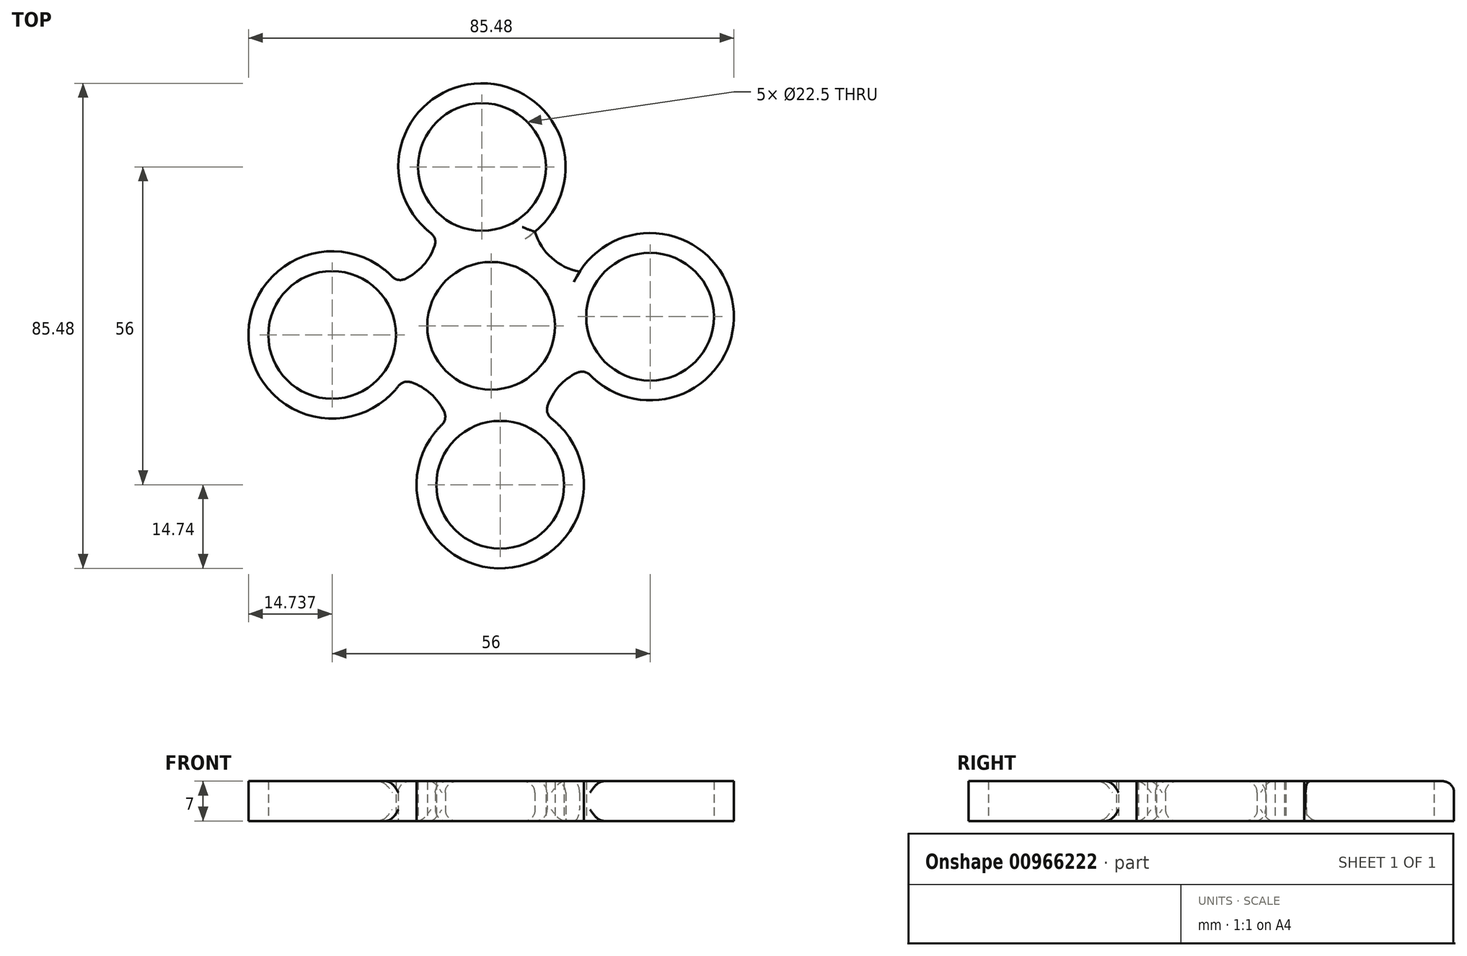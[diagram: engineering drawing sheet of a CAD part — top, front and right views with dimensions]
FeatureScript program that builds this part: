
annotation { "Feature Type Name" : "Feature", "Feature Type Description" : "" }
export const myFeature = defineFeature(function(context is Context, id is Id, definition is map)
    precondition{}
    {
        {
            var Q0;
            Q0=qCreatedBy(makeId("Top.planeOp"),FACE);
            var sketch = newSketch(context, id + "F0", { "sketchPlane" : qUnion([Q0])});
            skCircle(sketch, "E0", {"center": v(-7.42, 16.64) * mm, "radius": 11.25 * mm});
            skCircle(sketch, "E1", {"center": v(-9.03, 44.64) * mm, "radius": 11.25 * mm});
            skCircle(sketch, "E2.1.0", {"center": v(-35.42, 15.03) * mm, "radius": 11.25 * mm});
            skCircle(sketch, "E2.2.0", {"center": v(-5.82, -11.36) * mm, "radius": 11.25 * mm});
            skCircle(sketch, "E2.3.0", {"center": v(20.58, 18.25) * mm, "radius": 11.25 * mm});
            skArc(sketch, "E3", {"start": v(-28.83, 24.15) * mm, "mid": v(-19.39, 27.28) * mm, "end": v(-17.29, 37) * mm});
            skArc(sketch, "E4.1.0", {"start": v(-14.93, -4.76) * mm, "mid": v(-18.06, 4.67) * mm, "end": v(-27.78, 6.78) * mm});
            skArc(sketch, "E4.2.0", {"start": v(13.98, 9.13) * mm, "mid": v(4.54, 6) * mm, "end": v(2.44, -3.72) * mm});
            skArc(sketch, "E4.3.0", {"start": v(0.08, 38.04) * mm, "mid": v(3.22, 28.6) * mm, "end": v(12.94, 26.5) * mm});
            skCircle(sketch, "E5", {"center": v(-9.03, 44.64) * mm, "radius": 14.74 * mm});
            skCircle(sketch, "E6.1.0", {"center": v(-35.42, 15.03) * mm, "radius": 14.74 * mm});
            skCircle(sketch, "E6.2.0", {"center": v(-5.82, -11.36) * mm, "radius": 14.74 * mm});
            skCircle(sketch, "E6.3.0", {"center": v(20.58, 18.25) * mm, "radius": 14.74 * mm});
            skSolve(sketch);
        }
        {
            var Q0;
            {var subQ0=sQuery(id+"F0.wireOp",EDGE,"E3");var subQ1=sQuery(id+"F0.wireOp",EDGE,"E2.1.0");var subQ2=makeQuery(id+"F0.imprint","INTERSECT",VERTEX,{"derivedFrom":[subQ1,subQ0]});Q0=makeQuery(id+"F0.imprint","IMPRINT",FACE,{"disambiguationData":[TD([[makeQuery(id+"F0.imprint","IMPRINT",EDGE,{"disambiguationData":[TD([[subQ2,1.0]])],"derivedFrom":subQ1}),-1.0]])]});}
            var Q1;
            {var subQ0=sQuery(id+"F0.wireOp",EDGE,"E3");var subQ1=sQuery(id+"F0.wireOp",EDGE,"E2.1.0");var subQ2=makeQuery(id+"F0.imprint","INTERSECT",VERTEX,{"derivedFrom":[subQ1,subQ0]});Q1=makeQuery(id+"F0.imprint","IMPRINT",FACE,{"disambiguationData":[TD([[makeQuery(id+"F0.imprint","IMPRINT",EDGE,{"disambiguationData":[TD([[subQ2,-1.0]])],"derivedFrom":subQ1}),-1.0]])]});}
            var Q2;
            Q2=makeQuery(id+"F0.imprint","IMPRINT",FACE,{"disambiguationData":[TD([[makeQuery(id+"F0.imprint","IMPRINT",EDGE,{"derivedFrom":sQuery(id+"F0.wireOp",EDGE,"E0")}),-1.0]])]});
            var Q3;
            {var subQ0=sQuery(id+"F0.wireOp",EDGE,"E3");var subQ1=sQuery(id+"F0.wireOp",EDGE,"E1");var subQ2=makeQuery(id+"F0.imprint","INTERSECT",VERTEX,{"derivedFrom":[subQ1,subQ0]});Q3=makeQuery(id+"F0.imprint","IMPRINT",FACE,{"disambiguationData":[TD([[makeQuery(id+"F0.imprint","IMPRINT",EDGE,{"disambiguationData":[TD([[subQ2,-1.0]])],"derivedFrom":subQ1}),-1.0]])]});}
            var Q4;
            {var subQ0=sQuery(id+"F0.wireOp",EDGE,"E3");var subQ1=sQuery(id+"F0.wireOp",EDGE,"E1");var subQ2=makeQuery(id+"F0.imprint","INTERSECT",VERTEX,{"derivedFrom":[subQ1,subQ0]});Q4=makeQuery(id+"F0.imprint","IMPRINT",FACE,{"disambiguationData":[TD([[makeQuery(id+"F0.imprint","IMPRINT",EDGE,{"disambiguationData":[TD([[subQ2,1.0]])],"derivedFrom":subQ1}),-1.0]])]});}
            var Q5;
            {var subQ0=sQuery(id+"F0.wireOp",EDGE,"E4.2.0");var subQ1=sQuery(id+"F0.wireOp",EDGE,"E2.3.0");var subQ2=makeQuery(id+"F0.imprint","INTERSECT",VERTEX,{"derivedFrom":[subQ1,subQ0]});Q5=makeQuery(id+"F0.imprint","IMPRINT",FACE,{"disambiguationData":[TD([[makeQuery(id+"F0.imprint","IMPRINT",EDGE,{"disambiguationData":[TD([[subQ2,-1.0]])],"derivedFrom":subQ1}),-1.0]])]});}
            var Q6;
            {var subQ0=sQuery(id+"F0.wireOp",EDGE,"E4.2.0");var subQ1=sQuery(id+"F0.wireOp",EDGE,"E2.3.0");var subQ2=makeQuery(id+"F0.imprint","INTERSECT",VERTEX,{"derivedFrom":[subQ1,subQ0]});Q6=makeQuery(id+"F0.imprint","IMPRINT",FACE,{"disambiguationData":[TD([[makeQuery(id+"F0.imprint","IMPRINT",EDGE,{"disambiguationData":[TD([[subQ2,1.0]])],"derivedFrom":subQ1}),-1.0]])]});}
            var Q7;
            {var subQ0=sQuery(id+"F0.wireOp",EDGE,"E4.1.0");var subQ1=sQuery(id+"F0.wireOp",EDGE,"E2.2.0");var subQ2=makeQuery(id+"F0.imprint","INTERSECT",VERTEX,{"derivedFrom":[subQ1,subQ0]});Q7=makeQuery(id+"F0.imprint","IMPRINT",FACE,{"disambiguationData":[TD([[makeQuery(id+"F0.imprint","IMPRINT",EDGE,{"disambiguationData":[TD([[subQ2,1.0]])],"derivedFrom":subQ1}),-1.0]])]});}
            var Q8;
            {var subQ0=sQuery(id+"F0.wireOp",EDGE,"E4.1.0");var subQ1=sQuery(id+"F0.wireOp",EDGE,"E2.2.0");var subQ2=makeQuery(id+"F0.imprint","INTERSECT",VERTEX,{"derivedFrom":[subQ1,subQ0]});Q8=makeQuery(id+"F0.imprint","IMPRINT",FACE,{"disambiguationData":[TD([[makeQuery(id+"F0.imprint","IMPRINT",EDGE,{"disambiguationData":[TD([[subQ2,-1.0]])],"derivedFrom":subQ1}),-1.0]])]});}
            extrude(context, id + "F1", {"entities" : qUnion([Q0, Q1, Q2, Q3, Q4, Q5, Q6, Q7, Q8]), "depth" : 7 * mm, "offsetDistance" : 25 * mm});
        }
        {
            var Q0;
            Q0=makeQuery(id+"F1.opExtrude","CAP_EDGE",EDGE,{"disambiguationData":[OSD([sQuery(id+"F0.wireOp",EDGE,"E5")])],"isStart":false});
            var Q1;
            Q1=makeQuery(id+"F1.opExtrude","SWEPT_FACE",FACE,{"disambiguationData":[OSD([sQuery(id+"F0.wireOp",EDGE,"E3")])]});
            var Q2;
            Q2=makeQuery(id+"F1.opExtrude","SWEPT_FACE",FACE,{"disambiguationData":[OSD([sQuery(id+"F0.wireOp",EDGE,"E4.1.0")])]});
            var Q3;
            Q3=makeQuery(id+"F1.opExtrude","SWEPT_FACE",FACE,{"disambiguationData":[OSD([sQuery(id+"F0.wireOp",EDGE,"E4.2.0")])]});
            var Q4;
            Q4=makeQuery(id+"F1.opExtrude","CAP_EDGE",EDGE,{"disambiguationData":[OSD([sQuery(id+"F0.wireOp",EDGE,"E4.3.0")])],"isStart":false});
            var Q5;
            Q5=makeQuery(id+"F1.opExtrude","CAP_EDGE",EDGE,{"disambiguationData":[OSD([sQuery(id+"F0.wireOp",EDGE,"E4.3.0")])],"isStart":true});
            fillet(context, id + "F2", {"entities" : qUnion([Q0, Q1, Q2, Q3, Q4, Q5]), "radius" : 2 * mm, "tangentPropagation" : true, "allowEdgeOverflow" : false});
        }
    });
